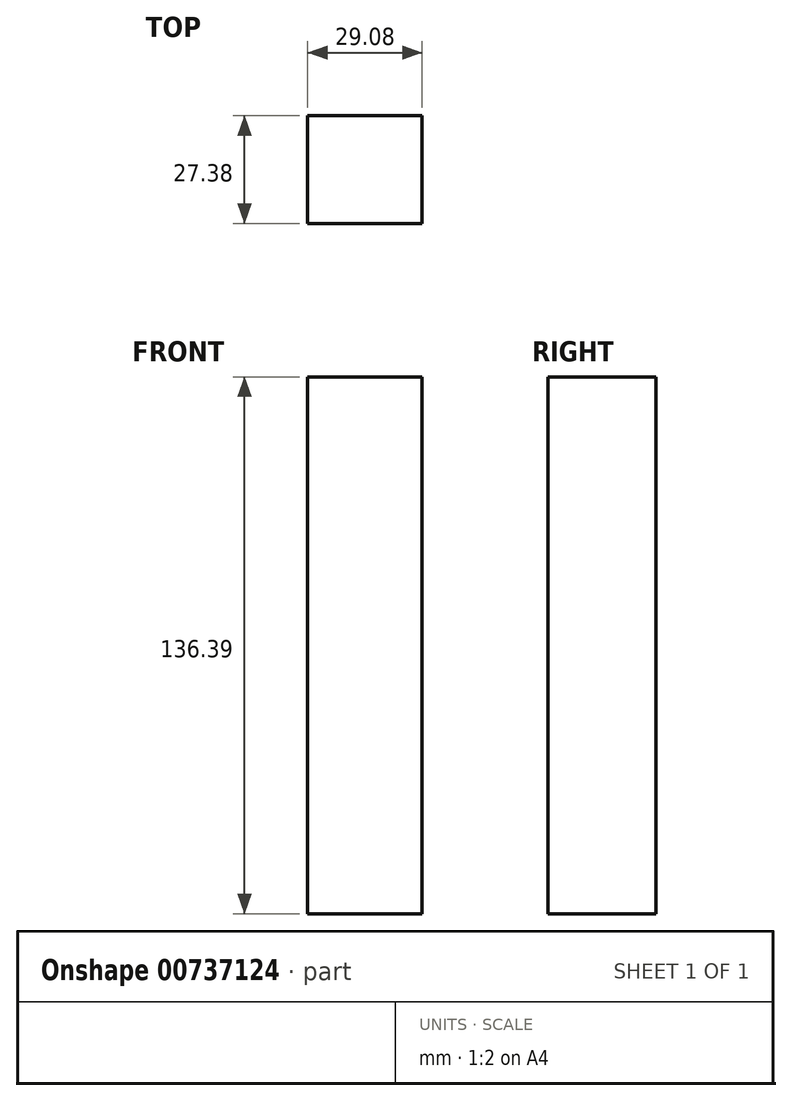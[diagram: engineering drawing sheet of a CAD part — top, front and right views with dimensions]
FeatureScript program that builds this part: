
annotation { "Feature Type Name" : "Feature", "Feature Type Description" : "" }
export const myFeature = defineFeature(function(context is Context, id is Id, definition is map)
    precondition{}
    {
        {
            var Q0;
            Q0=qCreatedBy(makeId("Top.planeOp"),FACE);
            var sketch = newSketch(context, id + "F0", { "sketchPlane" : qUnion([Q0])});
            skLineSegment(sketch, "E0.bottom", {"start": v(14.54, -13.69) * mm, "end": v(-14.54, -13.69) * mm});
            skLineSegment(sketch, "E0.top", {"start": v(14.54, 13.69) * mm, "end": v(-14.54, 13.69) * mm});
            skLineSegment(sketch, "E0.left", {"start": v(14.54, -13.69) * mm, "end": v(14.54, 13.69) * mm});
            skLineSegment(sketch, "E0.right", {"start": v(-14.54, -13.69) * mm, "end": v(-14.54, 13.69) * mm});
            skPoint(sketch, "E0.middle", {"position": v(0, 0) * mm});
            skSolve(sketch);
        }
        {
            var Q0;
            Q0 = qSketchRegion(id + "F0", true);
            extrude(context, id + "F1", {"entities" : qUnion([Q0]), "depth" : 136.4 * mm, "offsetDistance" : 25.4 * mm});
        }
    });
